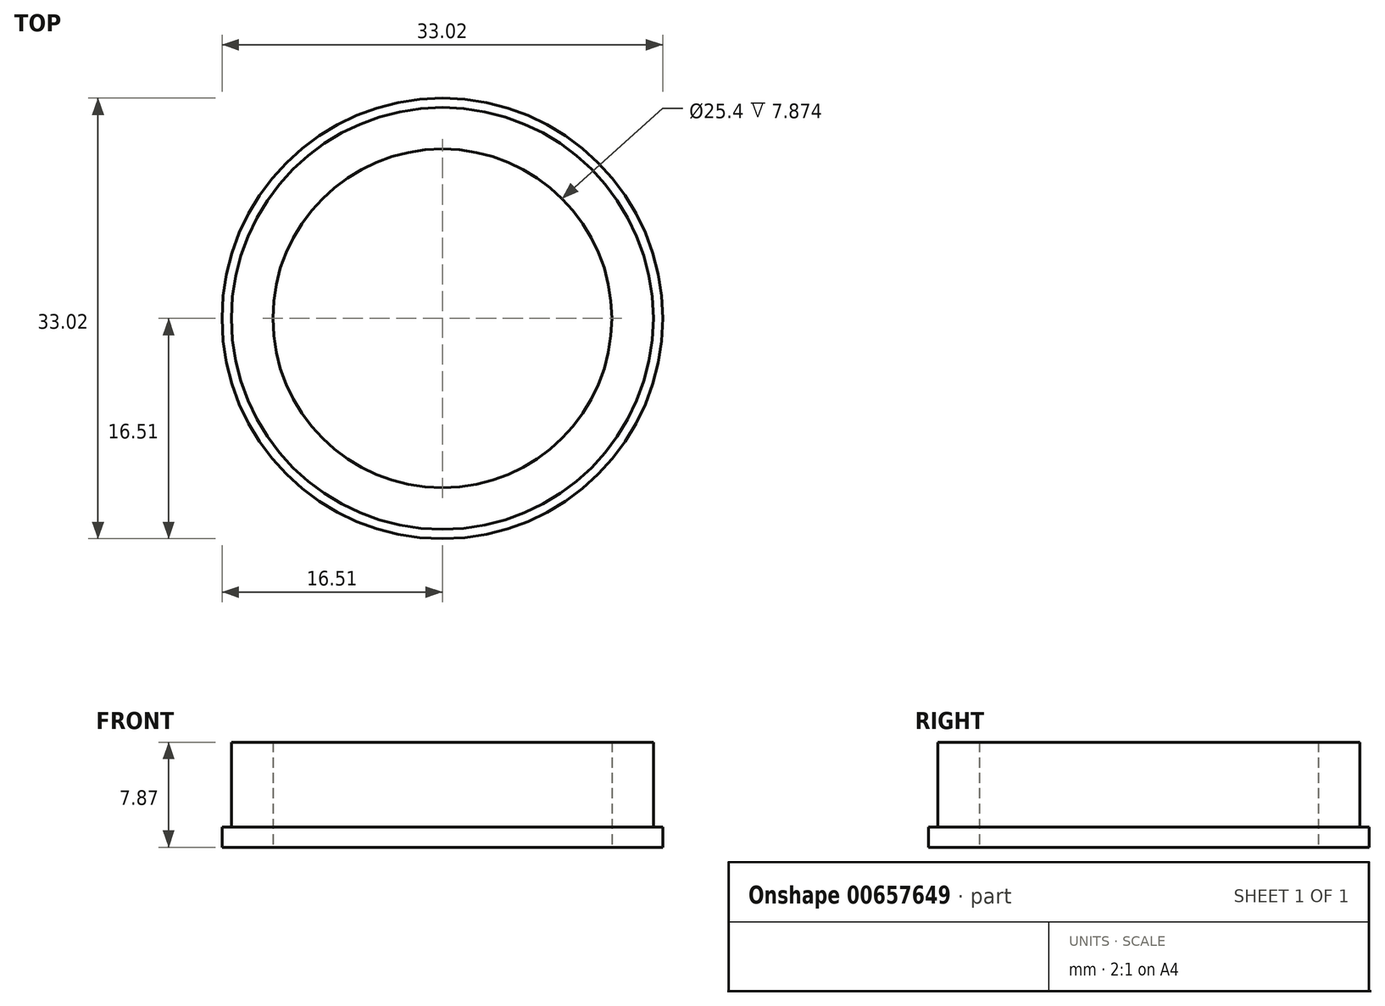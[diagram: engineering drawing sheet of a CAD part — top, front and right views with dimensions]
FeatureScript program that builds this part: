
annotation { "Feature Type Name" : "Feature", "Feature Type Description" : "" }
export const myFeature = defineFeature(function(context is Context, id is Id, definition is map)
    precondition{}
    {
        {
            var Q0;
            Q0=qCreatedBy(makeId("Top.planeOp"),FACE);
            var sketch = newSketch(context, id + "F0", { "sketchPlane" : qUnion([Q0])});
            skCircle(sketch, "E0", {"center": v(0, 0) * mm, "radius": 12.7 * mm});
            skCircle(sketch, "E1", {"center": v(0, 0) * mm, "radius": 15.81 * mm});
            skSolve(sketch);
        }
        {
            var Q0;
            Q0=makeQuery(id+"F0.imprint","IMPRINT",FACE,{"disambiguationData":[TD([[makeQuery(id+"F0.imprint","IMPRINT",EDGE,{"derivedFrom":sQuery(id+"F0.wireOp",EDGE,"E0")}),-1.0]])]});
            extrude(context, id + "F1", {"entities" : qUnion([Q0]), "depth" : 6.35 * mm, "offsetDistance" : 25.4 * mm});
        }
        {
            var Q0;
            Q0=makeQuery(id+"F1.opExtrude","CAP_FACE",FACE,{"disambiguationData":[OSD([sQuery(id+"F0.wireOp",EDGE,"E0"),sQuery(id+"F0.wireOp",EDGE,"E1")])],"isStart":true});
            var sketch = newSketch(context, id + "F2", { "sketchPlane" : qUnion([Q0])});
            skCircle(sketch, "E2", {"center": v(0, 0) * mm, "radius": 12.7 * mm});
            skCircle(sketch, "E3", {"center": v(0, 0) * mm, "radius": 16.51 * mm});
            skSolve(sketch);
        }
        {
            var Q0;
            Q0=makeQuery(id+"F2.imprint","IMPRINT",FACE,{"disambiguationData":[TD([[makeQuery(id+"F2.imprint","IMPRINT",EDGE,{"derivedFrom":sQuery(id+"F2.wireOp",EDGE,"E2")}),1.0]])]});
            var Q1;
            Q1=makeQuery(id+"F2.imprint","IMPRINT",FACE,{"disambiguationData":[TD([[makeQuery(id+"F2.imprint","IMPRINT",EDGE,{"derivedFrom":sQuery(id+"F2.wireOp",EDGE,"E3")}),1.0]])]});
            extrude(context, id + "F3", {"entities" : qUnion([Q0, Q1]), "operationType" : NewBodyOperationType.ADD, "depth" : 1.52 * mm, "offsetDistance" : 25.4 * mm});
        }
    });
